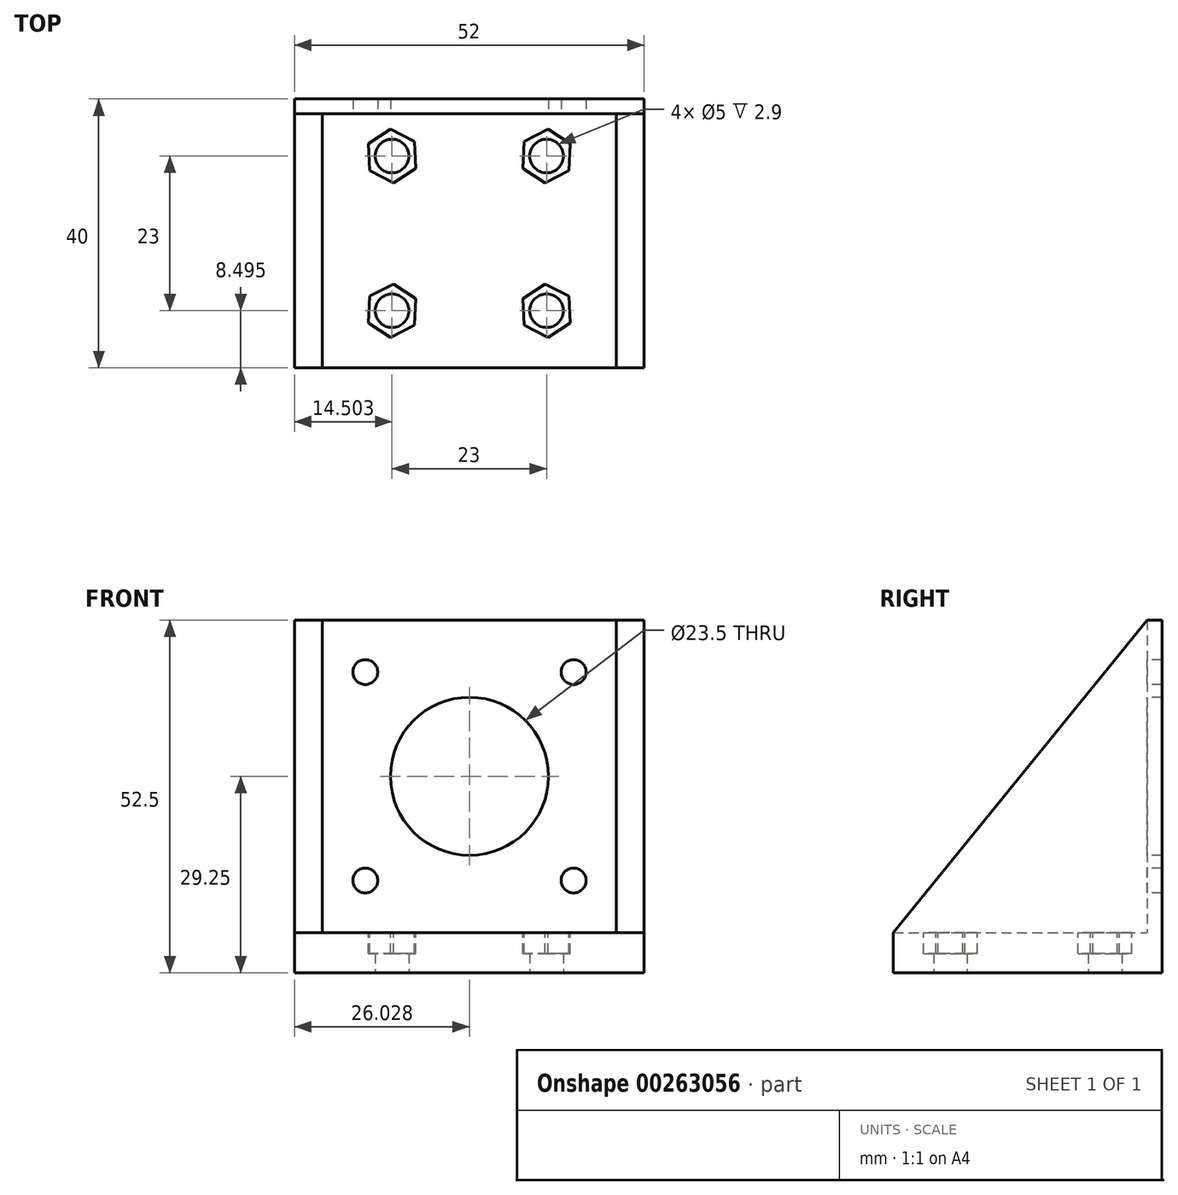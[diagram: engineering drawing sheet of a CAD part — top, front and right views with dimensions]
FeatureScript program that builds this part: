
annotation { "Feature Type Name" : "Feature", "Feature Type Description" : "" }
export const myFeature = defineFeature(function(context is Context, id is Id, definition is map)
    precondition{}
    {
        {
            var Q0;
            Q0=qCreatedBy(makeId("Top.planeOp"),FACE);
            var sketch = newSketch(context, id + "F0", { "sketchPlane" : qUnion([Q0])});
            skLineSegment(sketch, "E0.bottom", {"start": v(-23.99, -23.7) * mm, "end": v(28.01, -23.7) * mm});
            skLineSegment(sketch, "E0.top", {"start": v(-23.99, 16.3) * mm, "end": v(28.01, 16.3) * mm});
            skLineSegment(sketch, "E0.left", {"start": v(-23.99, -23.7) * mm, "end": v(-23.99, 16.3) * mm});
            skLineSegment(sketch, "E0.right", {"start": v(28.01, -23.7) * mm, "end": v(28.01, 16.3) * mm});
            skSolve(sketch);
        }
        {
            var Q0;
            Q0 = qSketchRegion(id + "F0", true);
            extrude(context, id + "F1", {"entities" : qUnion([Q0]), "depth" : 6 * mm});
        }
        {
            var Q0;
            Q0=makeQuery(id+"F1.opExtrude","CAP_FACE",FACE,{"disambiguationData":[OSD([sQuery(id+"F0.wireOp",EDGE,"E0.bottom"),sQuery(id+"F0.wireOp",EDGE,"E0.top"),sQuery(id+"F0.wireOp",EDGE,"E0.left"),sQuery(id+"F0.wireOp",EDGE,"E0.right")])],"isStart":false});
            var sketch = newSketch(context, id + "F2", { "sketchPlane" : qUnion([Q0])});
            skLineSegment(sketch, "E1.bottom", {"start": v(-23.99, 16.3) * mm, "end": v(28.01, 16.3) * mm});
            skLineSegment(sketch, "E1.top", {"start": v(-23.99, 14.1) * mm, "end": v(28.01, 14.1) * mm});
            skLineSegment(sketch, "E1.left", {"start": v(-23.99, 16.3) * mm, "end": v(-23.99, 14.1) * mm});
            skLineSegment(sketch, "E1.right", {"start": v(28.01, 16.3) * mm, "end": v(28.01, 14.1) * mm});
            skSolve(sketch);
        }
        {
            var Q0;
            Q0 = qSketchRegion(id + "F2", true);
            extrude(context, id + "F3", {"entities" : qUnion([Q0]), "operationType" : NewBodyOperationType.ADD, "depth" : (52.5 - 6) * mm});
        }
        {
            var Q0;
            Q0=makeQuery(id+"F3.boolean.opBoolean","MERGE",FACE,{"derivedFrom":[makeQuery(id+"F1.opExtrude","SWEPT_FACE",FACE,{"disambiguationData":[OSD([sQuery(id+"F0.wireOp",EDGE,"E0.right")])]}),makeQuery(id+"F3.opExtrude","SWEPT_FACE",FACE,{"disambiguationData":[OSD([sQuery(id+"F2.wireOp",EDGE,"E1.right")])]})]});
            var sketch = newSketch(context, id + "F4", { "sketchPlane" : qUnion([Q0])});
            skLineSegment(sketch, "E2", {"start": v(-23.7, 6) * mm, "end": v(14.1, 52.5) * mm});
            skLineSegment(sketch, "E3", {"start": v(14.1, 52.5) * mm, "end": v(14.1, 6) * mm});
            skLineSegment(sketch, "E4", {"start": v(14.1, 6) * mm, "end": v(-23.7, 6) * mm});
            skSolve(sketch);
        }
        {
            var Q0;
            Q0 = qSketchRegion(id + "F4", true);
            extrude(context, id + "F5", {"entities" : qUnion([Q0]), "operationType" : NewBodyOperationType.ADD, "oppositeDirection" : true, "depth" : 4.1 * mm});
        }
        {
            var Q0;
            Q0=makeQuery(id+"F3.boolean.opBoolean","MERGE",FACE,{"derivedFrom":[makeQuery(id+"F1.opExtrude","SWEPT_FACE",FACE,{"disambiguationData":[OSD([sQuery(id+"F0.wireOp",EDGE,"E0.left")])]}),makeQuery(id+"F3.opExtrude","SWEPT_FACE",FACE,{"disambiguationData":[OSD([sQuery(id+"F2.wireOp",EDGE,"E1.left")])]})]});
            var sketch = newSketch(context, id + "F6", { "sketchPlane" : qUnion([Q0])});
            skLineSegment(sketch, "E5", {"start": v(-14.1, 52.5) * mm, "end": v(23.7, 6) * mm});
            skLineSegment(sketch, "E6", {"start": v(23.7, 6) * mm, "end": v(-14.1, 6) * mm});
            skLineSegment(sketch, "E7", {"start": v(-14.1, 6) * mm, "end": v(-14.1, 52.5) * mm});
            skSolve(sketch);
        }
        {
            var Q0;
            Q0 = qSketchRegion(id + "F6", true);
            extrude(context, id + "F7", {"entities" : qUnion([Q0]), "operationType" : NewBodyOperationType.ADD, "oppositeDirection" : true, "depth" : 4.15 * mm});
        }
        {
            var Q0;
            Q0=makeQuery(id+"F3.opExtrude","SWEPT_FACE",FACE,{"disambiguationData":[OSD([sQuery(id+"F2.wireOp",EDGE,"E1.top")])]});
            var sketch = newSketch(context, id + "F8", { "sketchPlane" : qUnion([Q0])});
            skPoint(sketch, "E8.centerSnap0", {"position": v(-19.84, 29.25) * mm});
            skLineSegment(sketch, "E9", {"start": v(-19.84, 52.5) * mm, "end": v(23.91, 6) * mm, "construction": true});
            skCircle(sketch, "E10", {"center": v(2.04, 29.25) * mm, "radius": 11.75 * mm});
            skCircle(sketch, "E11", {"center": v(17.54, 44.75) * mm, "radius": 1.85 * mm});
            skLineSegment(sketch, "E12", {"start": v(2.04, 29.25) * mm, "end": v(17.54, 29.25) * mm, "construction": true});
            skLineSegment(sketch, "E13", {"start": v(2.04, 29.25) * mm, "end": v(2.04, 44.75) * mm, "construction": true});
            skCircle(sketch, "E14.MirrorC", {"center": v(-13.46, 44.75) * mm, "radius": 1.85 * mm});
            skCircle(sketch, "E15.MirrorC", {"center": v(-13.46, 13.75) * mm, "radius": 1.85 * mm});
            skCircle(sketch, "E16.MirrorC", {"center": v(17.54, 13.75) * mm, "radius": 1.85 * mm});
            skSolve(sketch);
        }
        {
            var Q0;
            Q0 = qSketchRegion(id + "F8", true);
            extrude(context, id + "F9", {"entities" : qUnion([Q0]), "operationType" : NewBodyOperationType.REMOVE, "oppositeDirection" : true, "depth" : 25 * mm});
        }
        {
            var Q0;
            Q0=makeQuery(id+"F1.opExtrude","CAP_FACE",FACE,{"disambiguationData":[OSD([sQuery(id+"F0.wireOp",EDGE,"E0.bottom"),sQuery(id+"F0.wireOp",EDGE,"E0.top"),sQuery(id+"F0.wireOp",EDGE,"E0.left"),sQuery(id+"F0.wireOp",EDGE,"E0.right")])],"isStart":true});
            var sketch = newSketch(context, id + "F10", { "sketchPlane" : qUnion([Q0])});
            skLineSegment(sketch, "E17", {"start": v(-23.99, -16.3) * mm, "end": v(28.01, 23.7) * mm, "construction": true});
            skLineSegment(sketch, "E18", {"start": v(2.01, 3.7) * mm, "end": v(13.51, 3.7) * mm, "construction": true});
            skLineSegment(sketch, "E19", {"start": v(2.01, 3.7) * mm, "end": v(2.01, 15.2) * mm, "construction": true});
            skCircle(sketch, "E20", {"center": v(13.51, 15.2) * mm, "radius": 2.5 * mm});
            skCircle(sketch, "E21.MirrorC", {"center": v(-9.49, 15.2) * mm, "radius": 2.5 * mm});
            skCircle(sketch, "E22.MirrorC", {"center": v(-9.49, -7.8) * mm, "radius": 2.5 * mm});
            skCircle(sketch, "E23.MirrorC", {"center": v(13.51, -7.8) * mm, "radius": 2.5 * mm});
            skSolve(sketch);
        }
        {
            var Q0;
            Q0 = qSketchRegion(id + "F10", true);
            extrude(context, id + "F11", {"entities" : qUnion([Q0]), "operationType" : NewBodyOperationType.REMOVE, "oppositeDirection" : true, "depth" : 25 * mm});
        }
        {
            var Q0;
            Q0=makeQuery(id+"F1.opExtrude","CAP_FACE",FACE,{"disambiguationData":[OSD([sQuery(id+"F0.wireOp",EDGE,"E0.bottom"),sQuery(id+"F0.wireOp",EDGE,"E0.top"),sQuery(id+"F0.wireOp",EDGE,"E0.left"),sQuery(id+"F0.wireOp",EDGE,"E0.right")])],"isStart":false});
            var sketch = newSketch(context, id + "F12", { "sketchPlane" : qUnion([Q0])});
            skCircle(sketch, "E24.cCircle", {"center": v(13.51, -15.2) * mm, "radius": 3.45 * mm, "construction": true});
            skLineSegment(sketch, "E24.0", {"start": v(9.97, -13.39) * mm, "end": v(13.31, -11.23) * mm});
            skLineSegment(sketch, "E24.1", {"start": v(13.31, -11.23) * mm, "end": v(16.86, -13.04) * mm});
            skLineSegment(sketch, "E24.2", {"start": v(16.86, -13.04) * mm, "end": v(17.06, -17.02) * mm});
            skLineSegment(sketch, "E24.3", {"start": v(17.06, -17.02) * mm, "end": v(13.71, -19.18) * mm});
            skLineSegment(sketch, "E24.4", {"start": v(13.71, -19.18) * mm, "end": v(10.17, -17.37) * mm});
            skLineSegment(sketch, "E24.5", {"start": v(10.17, -17.37) * mm, "end": v(9.97, -13.39) * mm});
            skPoint(sketch, "E24.0.midPoint", {"position": v(11.64, -12.3) * mm});
            skLineSegment(sketch, "E25", {"start": v(13.51, -15.2) * mm, "end": v(-9.49, 7.8) * mm, "construction": true});
            skLineSegment(sketch, "E26", {"start": v(2.01, -3.7) * mm, "end": v(2.01, -15.68) * mm, "construction": true});
            skLineSegment(sketch, "E27", {"start": v(2.01, -3.7) * mm, "end": v(11.87, -3.7) * mm, "construction": true});
            skLineSegment(sketch, "E28.MirrorCS", {"start": v(10.17, 9.96) * mm, "end": v(9.97, 5.98) * mm});
            skLineSegment(sketch, "E29.MirrorCS", {"start": v(13.71, 11.77) * mm, "end": v(10.17, 9.96) * mm});
            skLineSegment(sketch, "E30.MirrorCS", {"start": v(17.06, 9.61) * mm, "end": v(13.71, 11.77) * mm});
            skLineSegment(sketch, "E31.MirrorCS", {"start": v(16.86, 5.63) * mm, "end": v(17.06, 9.61) * mm});
            skLineSegment(sketch, "E32.MirrorCS", {"start": v(13.31, 3.82) * mm, "end": v(16.86, 5.63) * mm});
            skLineSegment(sketch, "E33.MirrorCS", {"start": v(9.97, 5.98) * mm, "end": v(13.31, 3.82) * mm});
            skCircle(sketch, "E34.MirrorC", {"center": v(13.51, 7.8) * mm, "radius": 3.45 * mm, "construction": true});
            skCircle(sketch, "E35.MirrorC", {"center": v(-9.49, -15.2) * mm, "radius": 3.45 * mm, "construction": true});
            skLineSegment(sketch, "E36.MirrorCS", {"start": v(-9.69, -19.18) * mm, "end": v(-6.14, -17.37) * mm});
            skLineSegment(sketch, "E37.MirrorCS", {"start": v(-13.03, -17.02) * mm, "end": v(-9.69, -19.18) * mm});
            skLineSegment(sketch, "E38.MirrorCS", {"start": v(-12.83, -13.04) * mm, "end": v(-13.03, -17.02) * mm});
            skLineSegment(sketch, "E39.MirrorCS", {"start": v(-9.29, -11.23) * mm, "end": v(-12.83, -13.04) * mm});
            skLineSegment(sketch, "E40.MirrorCS", {"start": v(-5.94, -13.39) * mm, "end": v(-9.29, -11.23) * mm});
            skLineSegment(sketch, "E41.MirrorCS", {"start": v(-6.14, -17.37) * mm, "end": v(-5.94, -13.39) * mm});
            skLineSegment(sketch, "E42.MirrorCS", {"start": v(-6.14, 9.96) * mm, "end": v(-5.94, 5.98) * mm});
            skLineSegment(sketch, "E43.MirrorCS", {"start": v(-9.69, 11.77) * mm, "end": v(-6.14, 9.96) * mm});
            skLineSegment(sketch, "E44.MirrorCS", {"start": v(-13.03, 9.61) * mm, "end": v(-9.69, 11.77) * mm});
            skLineSegment(sketch, "E45.MirrorCS", {"start": v(-12.83, 5.63) * mm, "end": v(-13.03, 9.61) * mm});
            skLineSegment(sketch, "E46.MirrorCS", {"start": v(-9.29, 3.82) * mm, "end": v(-12.83, 5.63) * mm});
            skCircle(sketch, "E47.MirrorC", {"center": v(-9.49, 7.8) * mm, "radius": 3.45 * mm, "construction": true});
            skLineSegment(sketch, "E48.MirrorCS", {"start": v(-5.94, 5.98) * mm, "end": v(-9.29, 3.82) * mm});
            skSolve(sketch);
        }
        {
            var Q0;
            Q0 = qSketchRegion(id + "F12", true);
            extrude(context, id + "F13", {"entities" : qUnion([Q0]), "operationType" : NewBodyOperationType.REMOVE, "oppositeDirection" : true, "depth" : 3.1 * mm});
        }
    });
